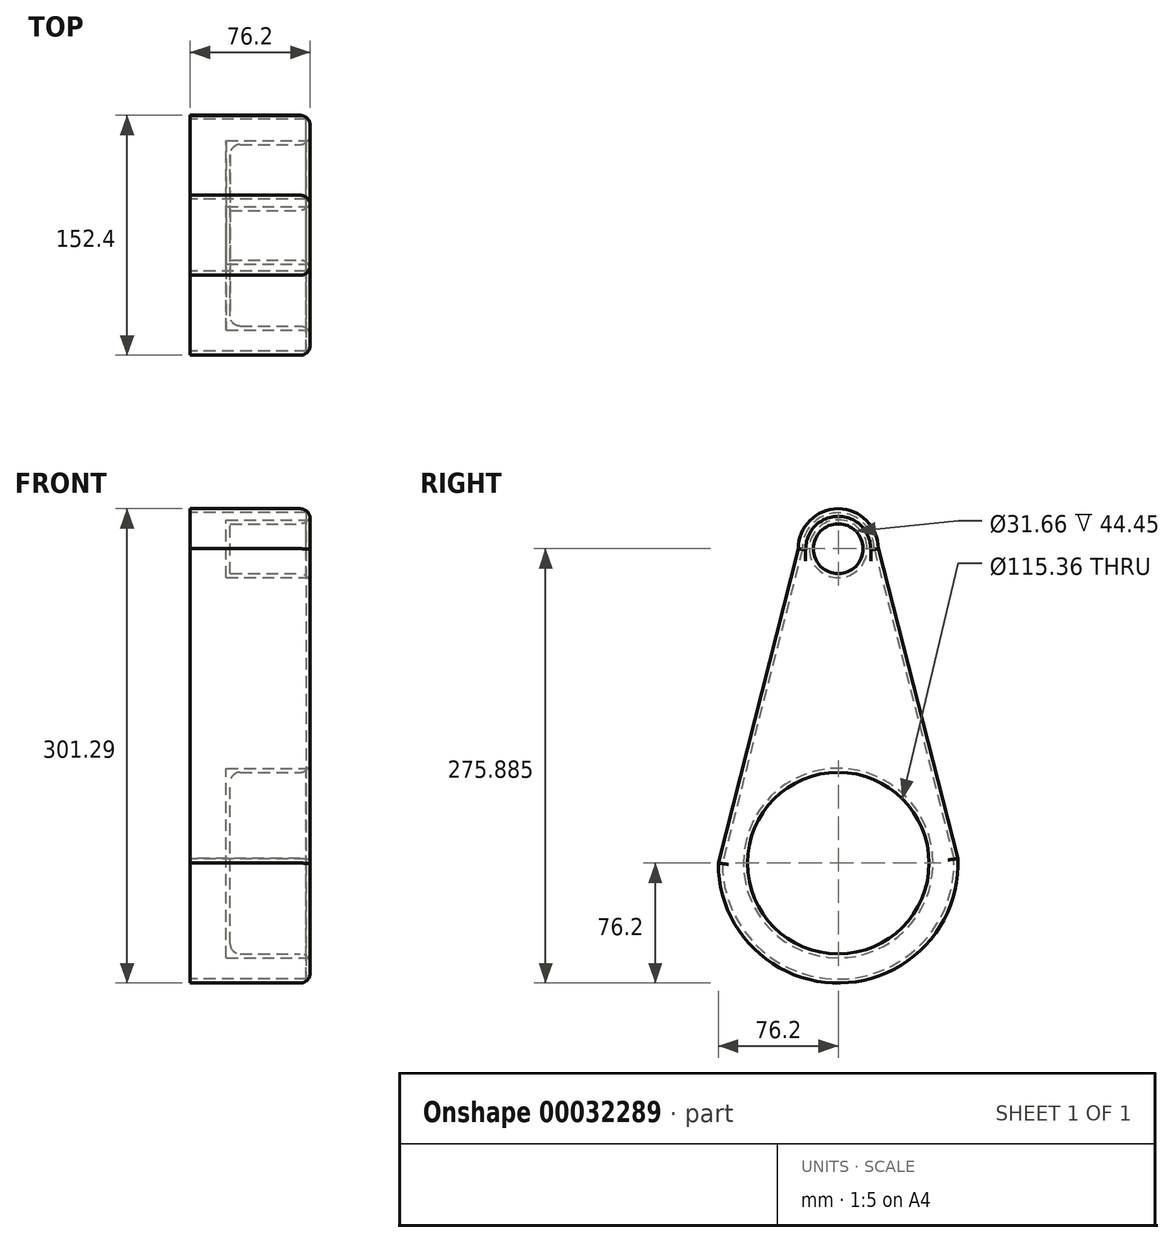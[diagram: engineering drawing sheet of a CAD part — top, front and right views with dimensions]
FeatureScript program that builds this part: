
annotation { "Feature Type Name" : "Feature", "Feature Type Description" : "" }
export const myFeature = defineFeature(function(context is Context, id is Id, definition is map)
    precondition{}
    {
        {
            var Q0;
            Q0=qCreatedBy(makeId("Right.planeOp"),FACE);
            var sketch = newSketch(context, id + "F0", { "sketchPlane" : qUnion([Q0])});
            skCircle(sketch, "E0", {"center": v(0, 0) * mm, "radius": 76.2 * mm});
            skCircle(sketch, "E1", {"center": v(0, 199.69) * mm, "radius": 25.4 * mm});
            skLineSegment(sketch, "E2", {"start": v(25.4, 199.69) * mm, "end": v(76.14, 2.92) * mm});
            skLineSegment(sketch, "E3", {"start": v(-25.4, 199.69) * mm, "end": v(-76.2, 0) * mm});
            skSolve(sketch);
        }
        {
            var Q0;
            {var subQ1=sQuery(id+"F0.wireOp",EDGE,"E0");var subQ4=sQuery(id+"F0.wireOp",EDGE,"E2");var subQ5=makeQuery(id+"F0.imprint","INTERSECT",VERTEX,{"disambiguationData":[OD(1.0)],"derivedFrom":[subQ1,subQ4]});Q0=makeQuery(id+"F0.imprint","IMPRINT",FACE,{"disambiguationData":[TD([[makeQuery(id+"F0.imprint","IMPRINT",EDGE,{"disambiguationData":[TD([[subQ5,-1.0]])],"derivedFrom":subQ1}),1.0]])]});}
            var Q1;
            {var subQ1=sQuery(id+"F0.wireOp",EDGE,"E0");var subQ5=sQuery(id+"F0.wireOp",EDGE,"E2");var subQ6=makeQuery(id+"F0.imprint","INTERSECT",VERTEX,{"disambiguationData":[OD(1.0)],"derivedFrom":[subQ1,subQ5]});Q1=makeQuery(id+"F0.imprint","IMPRINT",FACE,{"disambiguationData":[TD([[makeQuery(id+"F0.imprint","IMPRINT",EDGE,{"disambiguationData":[TD([[subQ6,-1.0]])],"derivedFrom":subQ1}),-1.0]])]});}
            var Q2;
            {var subQ0=sQuery(id+"F0.wireOp",EDGE,"E1");var subQ2=makeQuery(id+"F0.imprint","INTERSECT",VERTEX,{"derivedFrom":[subQ0,sQuery(id+"F0.wireOp",EDGE,"E2")]});Q2=makeQuery(id+"F0.imprint","IMPRINT",FACE,{"disambiguationData":[TD([[makeQuery(id+"F0.imprint","IMPRINT",EDGE,{"disambiguationData":[TD([[subQ2,-1.0]])],"derivedFrom":subQ0}),1.0]])]});}
            extrude(context, id + "F1", {"entities" : qUnion([Q0, Q1, Q2]), "depth" : 76.2 * mm});
        }
        {
            var Q0;
            Q0=makeQuery(id+"F1.opExtrude","CAP_FACE",FACE,{"disambiguationData":[OSD([sQuery(id+"F0.wireOp",EDGE,"E0"),sQuery(id+"F0.wireOp",EDGE,"E1"),sQuery(id+"F0.wireOp",EDGE,"E2"),sQuery(id+"F0.wireOp",EDGE,"E3")])],"isStart":false});
            var sketch = newSketch(context, id + "F2", { "sketchPlane" : qUnion([Q0])});
            skCircle(sketch, "E4", {"center": v(0, 0) * mm, "radius": 57.68 * mm});
            skCircle(sketch, "E5", {"center": v(0, 199.69) * mm, "radius": 15.83 * mm});
            skSolve(sketch);
        }
        {
            var Q0;
            Q0=makeQuery(id+"F2.imprint","IMPRINT",FACE,{"disambiguationData":[TD([[makeQuery(id+"F2.imprint","IMPRINT",EDGE,{"derivedFrom":sQuery(id+"F2.wireOp",EDGE,"E4")}),1.0]])]});
            var Q1;
            Q1=makeQuery(id+"F2.imprint","IMPRINT",FACE,{"disambiguationData":[TD([[makeQuery(id+"F2.imprint","IMPRINT",EDGE,{"derivedFrom":sQuery(id+"F2.wireOp",EDGE,"E5")}),1.0]])]});
            extrude(context, id + "F3", {"entities" : qUnion([Q0, Q1]), "operationType" : NewBodyOperationType.REMOVE, "oppositeDirection" : true, "depth" : 50.8 * mm});
        }
        {
            var Q0;
            Q0=makeQuery(id+"F1.opExtrude","CAP_FACE",FACE,{"disambiguationData":[OSD([sQuery(id+"F0.wireOp",EDGE,"E0"),sQuery(id+"F0.wireOp",EDGE,"E1"),sQuery(id+"F0.wireOp",EDGE,"E2"),sQuery(id+"F0.wireOp",EDGE,"E3")])],"isStart":true});
            shell(context, id + "F4", {"entities" : qUnion([Q0]), "thickness" : 2.54 * mm});
        }
        {
            var Q0;
            Q0=makeQuery(id+"F1.opExtrude","CAP_FACE",FACE,{"disambiguationData":[OSD([sQuery(id+"F0.wireOp",EDGE,"E0"),sQuery(id+"F0.wireOp",EDGE,"E1"),sQuery(id+"F0.wireOp",EDGE,"E2"),sQuery(id+"F0.wireOp",EDGE,"E3")])],"isStart":false});
            var Q1;
            Q1=makeQuery(id+"F3.boolean.opBoolean","COPY",EDGE,{"derivedFrom":makeQuery(id+"F3.opExtrude","CAP_EDGE",EDGE,{"disambiguationData":[OSD([sQuery(id+"F2.wireOp",EDGE,"E4")])],"isStart":false})});
            fillet(context, id + "F5", {"entities" : qUnion([Q0, Q1]), "radius" : 6.35 * mm, "tangentPropagation" : true, "allowEdgeOverflow" : false});
        }
    });
